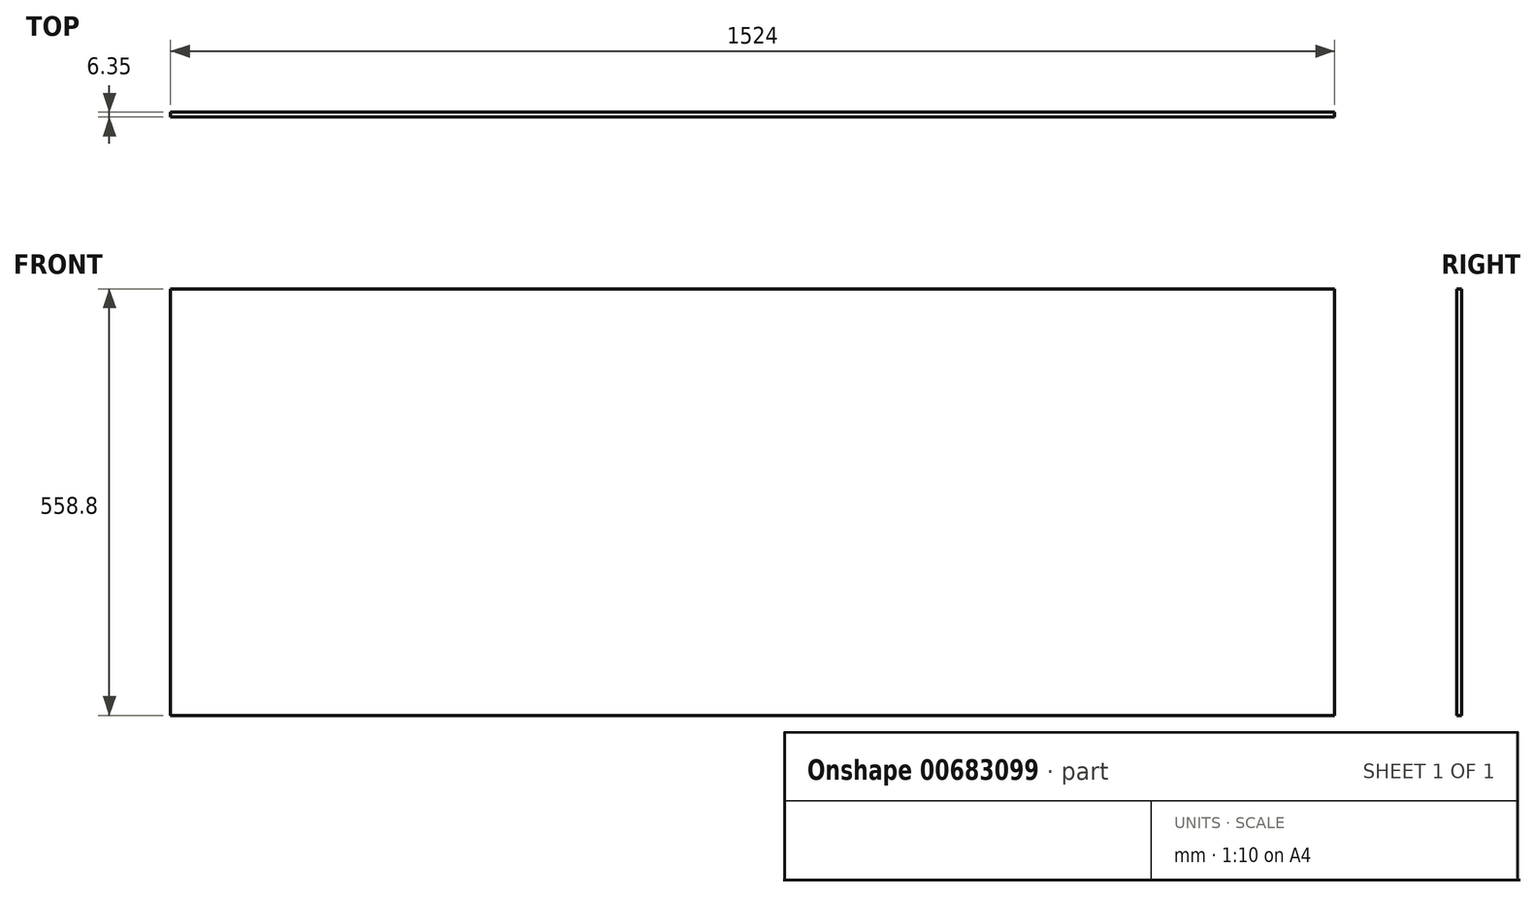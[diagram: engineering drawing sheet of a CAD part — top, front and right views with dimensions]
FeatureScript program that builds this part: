
annotation { "Feature Type Name" : "Feature", "Feature Type Description" : "" }
export const myFeature = defineFeature(function(context is Context, id is Id, definition is map)
    precondition{}
    {
        {
            var Q0;
            Q0=qCreatedBy(makeId("Front.planeOp"),FACE);
            var sketch = newSketch(context, id + "F0", { "sketchPlane" : qUnion([Q0])});
            skLineSegment(sketch, "E0.bottom", {"start": v(-762, 279.4) * mm, "end": v(762, 279.4) * mm});
            skLineSegment(sketch, "E0.top", {"start": v(-762, -279.4) * mm, "end": v(762, -279.4) * mm});
            skLineSegment(sketch, "E0.left", {"start": v(-762, 279.4) * mm, "end": v(-762, -279.4) * mm});
            skLineSegment(sketch, "E0.right", {"start": v(762, 279.4) * mm, "end": v(762, -279.4) * mm});
            skPoint(sketch, "E0.middle", {"position": v(0, 0) * mm});
            skSolve(sketch);
        }
        {
            var Q0;
            Q0 = qSketchRegion(id + "F0", true);
            extrude(context, id + "F1", {"entities" : qUnion([Q0]), "depth" : 6.35 * mm, "offsetDistance" : 25.4 * mm});
        }
    });
